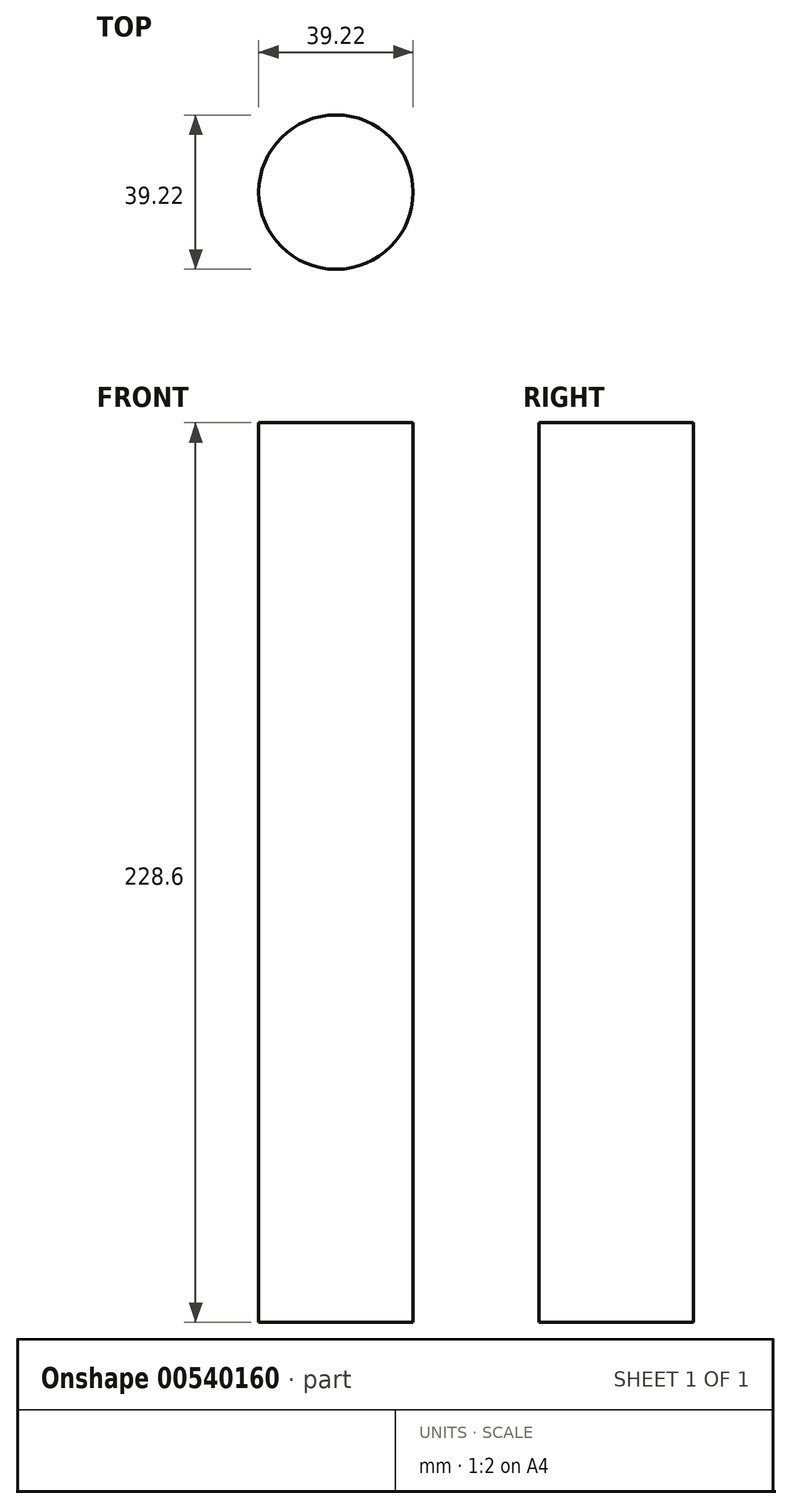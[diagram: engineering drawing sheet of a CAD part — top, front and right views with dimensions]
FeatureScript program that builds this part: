
annotation { "Feature Type Name" : "Feature", "Feature Type Description" : "" }
export const myFeature = defineFeature(function(context is Context, id is Id, definition is map)
    precondition{}
    {
        {
            var Q0;
            Q0=qCreatedBy(makeId("Top.planeOp"),FACE);
            var sketch = newSketch(context, id + "F0", { "sketchPlane" : qUnion([Q0])});
            skCircle(sketch, "E0", {"center": v(0, 0) * mm, "radius": 19.6 * mm});
            skSolve(sketch);
        }
        {
            var Q0;
            Q0 = qSketchRegion(id + "F0", true);
            extrude(context, id + "F1", {"entities" : qUnion([Q0]), "depth" : 228.6 * mm, "offsetDistance" : 25.4 * mm});
        }
    });
